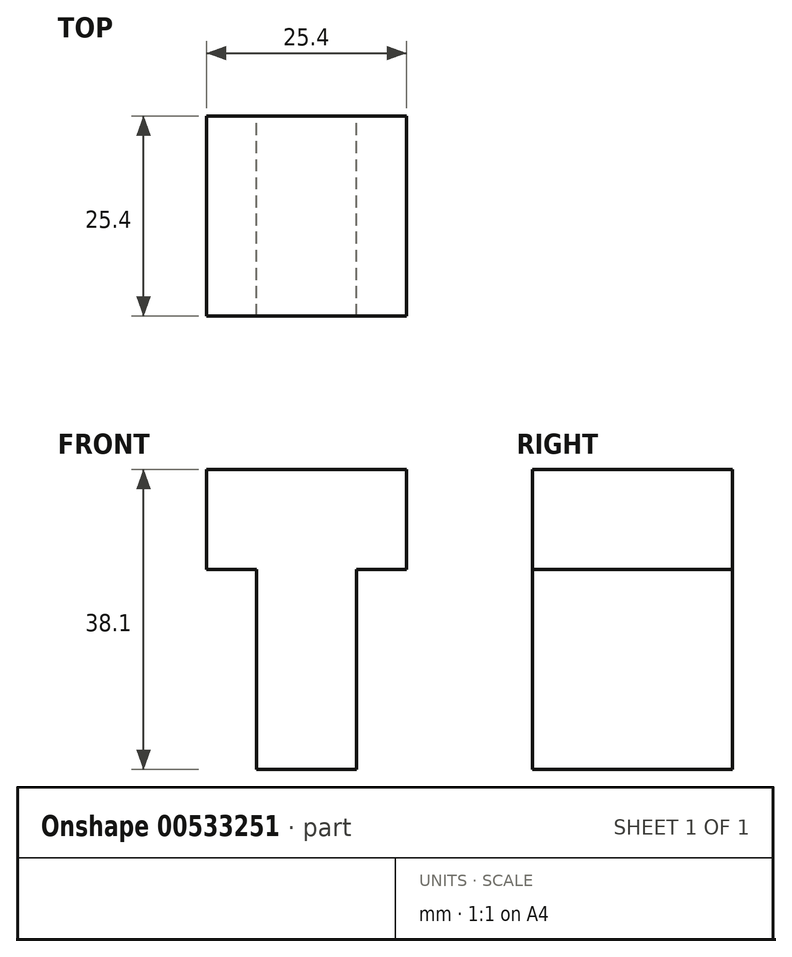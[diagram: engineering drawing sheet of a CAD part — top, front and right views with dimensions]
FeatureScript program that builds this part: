
annotation { "Feature Type Name" : "Feature", "Feature Type Description" : "" }
export const myFeature = defineFeature(function(context is Context, id is Id, definition is map)
    precondition{}
    {
        {
            var Q0;
            Q0=qCreatedBy(makeId("Front.planeOp"),FACE);
            var sketch = newSketch(context, id + "F0", { "sketchPlane" : qUnion([Q0])});
            skLineSegment(sketch, "E0", {"start": v(-53.65, 40.54) * mm, "end": v(-28.25, 40.54) * mm});
            skLineSegment(sketch, "E1", {"start": v(-28.25, 40.54) * mm, "end": v(-28.25, 27.84) * mm});
            skLineSegment(sketch, "E2", {"start": v(-53.65, 40.54) * mm, "end": v(-53.65, 27.84) * mm});
            skLineSegment(sketch, "E3", {"start": v(-53.65, 27.84) * mm, "end": v(-47.3, 27.84) * mm});
            skLineSegment(sketch, "E4", {"start": v(-28.25, 27.84) * mm, "end": v(-34.6, 27.84) * mm});
            skLineSegment(sketch, "E5", {"start": v(-47.3, 27.84) * mm, "end": v(-47.3, 2.44) * mm});
            skLineSegment(sketch, "E6", {"start": v(-34.6, 27.84) * mm, "end": v(-34.6, 2.44) * mm});
            skLineSegment(sketch, "E7", {"start": v(-47.3, 2.44) * mm, "end": v(-34.6, 2.44) * mm});
            skSolve(sketch);
        }
        {
            var Q0;
            Q0 = qSketchRegion(id + "F0", true);
            extrude(context, id + "F1", {"entities" : qUnion([Q0]), "depth" : 25.4 * mm, "offsetDistance" : 25.4 * mm});
        }
    });
